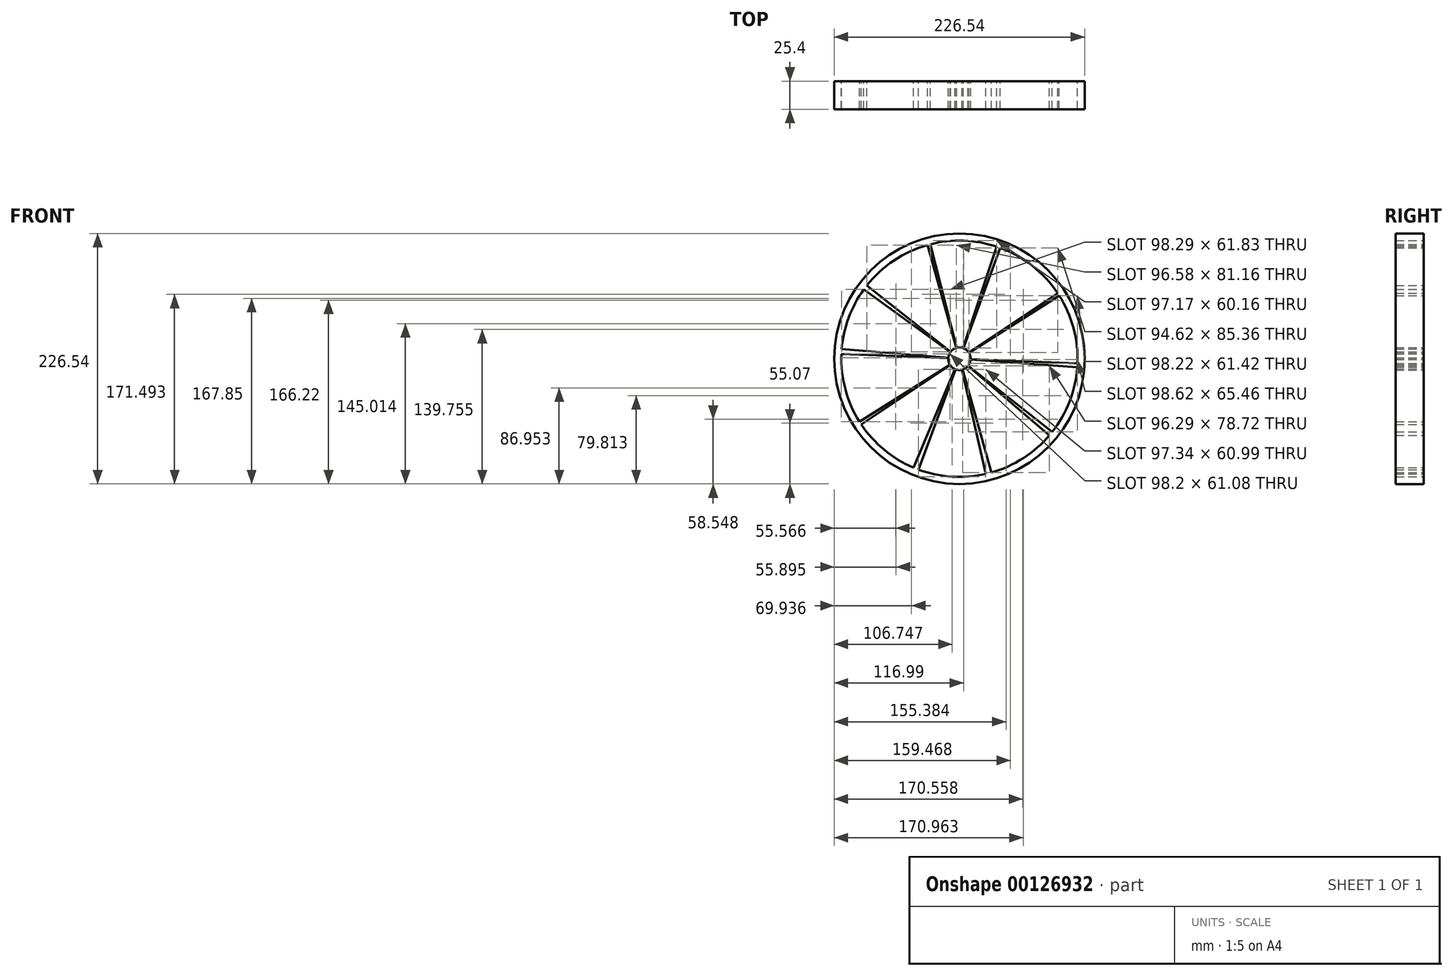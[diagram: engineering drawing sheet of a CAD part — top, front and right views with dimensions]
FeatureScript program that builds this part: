
annotation { "Feature Type Name" : "Feature", "Feature Type Description" : "" }
export const myFeature = defineFeature(function(context is Context, id is Id, definition is map)
    precondition{}
    {
        {
            var Q0;
            Q0=qCreatedBy(makeId("Front.planeOp"),FACE);
            var sketch = newSketch(context, id + "F0", { "sketchPlane" : qUnion([Q0])});
            skCircle(sketch, "E0", {"center": v(0, 0) * mm, "radius": 10.16 * mm});
            skCircle(sketch, "E1.cCircle", {"center": v(0, 0) * mm, "radius": 107.5 * mm, "construction": true});
            skLineSegment(sketch, "E1.0", {"start": v(-104.75, -29.51) * mm, "end": v(-108.75, 4.3) * mm});
            skLineSegment(sketch, "E1.1", {"start": v(-108.75, 4.3) * mm, "end": v(-102.1, 37.7) * mm});
            skLineSegment(sketch, "E1.2", {"start": v(-102.1, 37.7) * mm, "end": v(-85.45, 67.4) * mm});
            skLineSegment(sketch, "E1.3", {"start": v(-85.45, 67.4) * mm, "end": v(-60.44, 90.5) * mm});
            skLineSegment(sketch, "E1.4", {"start": v(-60.44, 90.5) * mm, "end": v(-29.51, 104.75) * mm});
            skLineSegment(sketch, "E1.5", {"start": v(-29.51, 104.75) * mm, "end": v(4.3, 108.75) * mm});
            skLineSegment(sketch, "E1.6", {"start": v(4.3, 108.75) * mm, "end": v(37.7, 102.1) * mm});
            skLineSegment(sketch, "E1.7", {"start": v(37.7, 102.1) * mm, "end": v(67.4, 85.45) * mm});
            skLineSegment(sketch, "E1.8", {"start": v(67.4, 85.45) * mm, "end": v(90.5, 60.44) * mm});
            skLineSegment(sketch, "E1.9", {"start": v(90.5, 60.44) * mm, "end": v(104.75, 29.51) * mm});
            skLineSegment(sketch, "E1.10", {"start": v(104.75, 29.51) * mm, "end": v(108.75, -4.3) * mm});
            skLineSegment(sketch, "E1.11", {"start": v(108.75, -4.3) * mm, "end": v(102.1, -37.7) * mm});
            skLineSegment(sketch, "E1.12", {"start": v(102.1, -37.7) * mm, "end": v(85.45, -67.4) * mm});
            skLineSegment(sketch, "E1.13", {"start": v(85.45, -67.4) * mm, "end": v(60.44, -90.5) * mm});
            skLineSegment(sketch, "E1.14", {"start": v(60.44, -90.5) * mm, "end": v(29.51, -104.75) * mm});
            skLineSegment(sketch, "E1.15", {"start": v(29.51, -104.75) * mm, "end": v(-4.3, -108.75) * mm});
            skLineSegment(sketch, "E1.16", {"start": v(-4.3, -108.75) * mm, "end": v(-37.7, -102.1) * mm});
            skLineSegment(sketch, "E1.17", {"start": v(-37.7, -102.1) * mm, "end": v(-67.4, -85.45) * mm});
            skLineSegment(sketch, "E1.18", {"start": v(-67.4, -85.45) * mm, "end": v(-90.5, -60.44) * mm});
            skLineSegment(sketch, "E1.19", {"start": v(-90.5, -60.44) * mm, "end": v(-104.75, -29.51) * mm});
            skPoint(sketch, "E1.0.midPoint", {"position": v(-106.75, -12.6) * mm});
            skCircle(sketch, "E2", {"center": v(0, 0) * mm, "radius": 106.87 * mm});
            skCircle(sketch, "E3", {"center": v(0, 0) * mm, "radius": 113.27 * mm});
            skLineSegment(sketch, "E4", {"start": v(-29.51, 104.75) * mm, "end": v(0, 0) * mm});
            skLineSegment(sketch, "E5", {"start": v(0, 0) * mm, "end": v(-26.74, 105.08) * mm});
            skLineSegment(sketch, "E6", {"start": v(37.7, 102.1) * mm, "end": v(0, 0) * mm});
            skLineSegment(sketch, "E7", {"start": v(0, 0) * mm, "end": v(34.26, 102.78) * mm});
            skLineSegment(sketch, "E8", {"start": v(0, 0) * mm, "end": v(90.5, 60.44) * mm});
            skLineSegment(sketch, "E9", {"start": v(0, 0) * mm, "end": v(91.61, 58.04) * mm});
            skLineSegment(sketch, "E10", {"start": v(0, 0) * mm, "end": v(108.75, -4.3) * mm});
            skLineSegment(sketch, "E11", {"start": v(0, 0) * mm, "end": v(108.06, -7.76) * mm});
            skLineSegment(sketch, "E12", {"start": v(0, 0) * mm, "end": v(85.45, -67.4) * mm});
            skLineSegment(sketch, "E13", {"start": v(0, 0) * mm, "end": v(81.47, -69.17) * mm});
            skLineSegment(sketch, "E14", {"start": v(0, 0) * mm, "end": v(29.51, -104.75) * mm});
            skLineSegment(sketch, "E15", {"start": v(0, 0) * mm, "end": v(24.1, -104.75) * mm});
            skLineSegment(sketch, "E16", {"start": v(0, 0) * mm, "end": v(-37.7, -102.1) * mm});
            skLineSegment(sketch, "E17", {"start": v(0, 0) * mm, "end": v(-41.43, -98.52) * mm});
            skLineSegment(sketch, "E18", {"start": v(0, 0) * mm, "end": v(-90.5, -60.44) * mm});
            skLineSegment(sketch, "E19", {"start": v(0, 0) * mm, "end": v(-91.78, -57.67) * mm});
            skLineSegment(sketch, "E20", {"start": v(0, 0) * mm, "end": v(-85.45, 67.4) * mm});
            skLineSegment(sketch, "E21", {"start": v(0, 0) * mm, "end": v(-87.67, 63.45) * mm});
            skLineSegment(sketch, "E22", {"start": v(0, 0) * mm, "end": v(-108.75, 4.3) * mm});
            skLineSegment(sketch, "E23", {"start": v(0, 0) * mm, "end": v(-107.85, 8.8) * mm});
            skSolve(sketch);
        }
        {
            var Q0;
            {var subQ0=sQuery(id+"F0.wireOp",EDGE,"E8");var subQ1=sQuery(id+"F0.wireOp",EDGE,"E0");var subQ2=makeQuery(id+"F0.imprint","INTERSECT",VERTEX,{"derivedFrom":[subQ1,subQ0]});Q0=makeQuery(id+"F0.imprint","IMPRINT",FACE,{"disambiguationData":[TD([[makeQuery(id+"F0.imprint","IMPRINT",EDGE,{"disambiguationData":[TD([[subQ2,-1.0]])],"derivedFrom":subQ1}),1.0]])]});}
            var Q1;
            {var subQ0=sQuery(id+"F0.wireOp",EDGE,"E7");var subQ1=sQuery(id+"F0.wireOp",EDGE,"E0");var subQ2=makeQuery(id+"F0.imprint","INTERSECT",VERTEX,{"derivedFrom":[subQ1,subQ0]});Q1=makeQuery(id+"F0.imprint","IMPRINT",FACE,{"disambiguationData":[TD([[makeQuery(id+"F0.imprint","IMPRINT",EDGE,{"disambiguationData":[TD([[subQ2,-1.0]])],"derivedFrom":subQ1}),1.0]])]});}
            var Q2;
            {var subQ0=sQuery(id+"F0.wireOp",EDGE,"E4");var subQ1=sQuery(id+"F0.wireOp",EDGE,"E0");var subQ2=makeQuery(id+"F0.imprint","INTERSECT",VERTEX,{"derivedFrom":[subQ1,subQ0]});Q2=makeQuery(id+"F0.imprint","IMPRINT",FACE,{"disambiguationData":[TD([[makeQuery(id+"F0.imprint","IMPRINT",EDGE,{"disambiguationData":[TD([[subQ2,-1.0]])],"derivedFrom":subQ1}),1.0]])]});}
            var Q3;
            {var subQ0=sQuery(id+"F0.wireOp",EDGE,"E21");var subQ1=sQuery(id+"F0.wireOp",EDGE,"E0");var subQ2=makeQuery(id+"F0.imprint","INTERSECT",VERTEX,{"derivedFrom":[subQ1,subQ0]});Q3=makeQuery(id+"F0.imprint","IMPRINT",FACE,{"disambiguationData":[TD([[makeQuery(id+"F0.imprint","IMPRINT",EDGE,{"disambiguationData":[TD([[subQ2,-1.0]])],"derivedFrom":subQ1}),1.0]])]});}
            var Q4;
            {var subQ0=sQuery(id+"F0.wireOp",EDGE,"E22");var subQ1=sQuery(id+"F0.wireOp",EDGE,"E0");var subQ2=makeQuery(id+"F0.imprint","INTERSECT",VERTEX,{"derivedFrom":[subQ1,subQ0]});Q4=makeQuery(id+"F0.imprint","IMPRINT",FACE,{"disambiguationData":[TD([[makeQuery(id+"F0.imprint","IMPRINT",EDGE,{"disambiguationData":[TD([[subQ2,-1.0]])],"derivedFrom":subQ1}),1.0]])]});}
            var Q5;
            {var subQ0=sQuery(id+"F0.wireOp",EDGE,"E16");var subQ1=sQuery(id+"F0.wireOp",EDGE,"E0");var subQ2=makeQuery(id+"F0.imprint","INTERSECT",VERTEX,{"derivedFrom":[subQ1,subQ0]});Q5=makeQuery(id+"F0.imprint","IMPRINT",FACE,{"disambiguationData":[TD([[makeQuery(id+"F0.imprint","IMPRINT",EDGE,{"disambiguationData":[TD([[subQ2,-1.0]])],"derivedFrom":subQ1}),1.0]])]});}
            var Q6;
            {var subQ0=sQuery(id+"F0.wireOp",EDGE,"E14");var subQ1=sQuery(id+"F0.wireOp",EDGE,"E0");var subQ2=makeQuery(id+"F0.imprint","INTERSECT",VERTEX,{"derivedFrom":[subQ1,subQ0]});Q6=makeQuery(id+"F0.imprint","IMPRINT",FACE,{"disambiguationData":[TD([[makeQuery(id+"F0.imprint","IMPRINT",EDGE,{"disambiguationData":[TD([[subQ2,-1.0]])],"derivedFrom":subQ1}),1.0]])]});}
            var Q7;
            {var subQ0=sQuery(id+"F0.wireOp",EDGE,"E12");var subQ1=sQuery(id+"F0.wireOp",EDGE,"E0");var subQ2=makeQuery(id+"F0.imprint","INTERSECT",VERTEX,{"derivedFrom":[subQ1,subQ0]});Q7=makeQuery(id+"F0.imprint","IMPRINT",FACE,{"disambiguationData":[TD([[makeQuery(id+"F0.imprint","IMPRINT",EDGE,{"disambiguationData":[TD([[subQ2,-1.0]])],"derivedFrom":subQ1}),1.0]])]});}
            var Q8;
            {var subQ0=sQuery(id+"F0.wireOp",EDGE,"E5");var subQ1=sQuery(id+"F0.wireOp",EDGE,"E0");var subQ2=makeQuery(id+"F0.imprint","INTERSECT",VERTEX,{"derivedFrom":[subQ1,subQ0]});Q8=makeQuery(id+"F0.imprint","IMPRINT",FACE,{"disambiguationData":[TD([[makeQuery(id+"F0.imprint","IMPRINT",EDGE,{"disambiguationData":[TD([[subQ2,-1.0]])],"derivedFrom":subQ1}),1.0]])]});}
            var Q9;
            {var subQ0=sQuery(id+"F0.wireOp",EDGE,"E20");var subQ1=sQuery(id+"F0.wireOp",EDGE,"E0");var subQ2=makeQuery(id+"F0.imprint","INTERSECT",VERTEX,{"derivedFrom":[subQ1,subQ0]});Q9=makeQuery(id+"F0.imprint","IMPRINT",FACE,{"disambiguationData":[TD([[makeQuery(id+"F0.imprint","IMPRINT",EDGE,{"disambiguationData":[TD([[subQ2,-1.0]])],"derivedFrom":subQ1}),1.0]])]});}
            var Q10;
            {var subQ0=sQuery(id+"F0.wireOp",EDGE,"E23");var subQ1=sQuery(id+"F0.wireOp",EDGE,"E0");var subQ2=makeQuery(id+"F0.imprint","INTERSECT",VERTEX,{"derivedFrom":[subQ1,subQ0]});Q10=makeQuery(id+"F0.imprint","IMPRINT",FACE,{"disambiguationData":[TD([[makeQuery(id+"F0.imprint","IMPRINT",EDGE,{"disambiguationData":[TD([[subQ2,-1.0]])],"derivedFrom":subQ1}),1.0]])]});}
            var Q11;
            {var subQ0=sQuery(id+"F0.wireOp",EDGE,"E19");var subQ1=sQuery(id+"F0.wireOp",EDGE,"E0");var subQ2=makeQuery(id+"F0.imprint","INTERSECT",VERTEX,{"derivedFrom":[subQ1,subQ0]});Q11=makeQuery(id+"F0.imprint","IMPRINT",FACE,{"disambiguationData":[TD([[makeQuery(id+"F0.imprint","IMPRINT",EDGE,{"disambiguationData":[TD([[subQ2,-1.0]])],"derivedFrom":subQ1}),1.0]])]});}
            var Q12;
            {var subQ0=sQuery(id+"F0.wireOp",EDGE,"E18");var subQ1=sQuery(id+"F0.wireOp",EDGE,"E0");var subQ2=makeQuery(id+"F0.imprint","INTERSECT",VERTEX,{"derivedFrom":[subQ1,subQ0]});Q12=makeQuery(id+"F0.imprint","IMPRINT",FACE,{"disambiguationData":[TD([[makeQuery(id+"F0.imprint","IMPRINT",EDGE,{"disambiguationData":[TD([[subQ2,-1.0]])],"derivedFrom":subQ1}),1.0]])]});}
            var Q13;
            {var subQ0=sQuery(id+"F0.wireOp",EDGE,"E15");var subQ1=sQuery(id+"F0.wireOp",EDGE,"E0");var subQ2=makeQuery(id+"F0.imprint","INTERSECT",VERTEX,{"derivedFrom":[subQ1,subQ0]});Q13=makeQuery(id+"F0.imprint","IMPRINT",FACE,{"disambiguationData":[TD([[makeQuery(id+"F0.imprint","IMPRINT",EDGE,{"disambiguationData":[TD([[subQ2,-1.0]])],"derivedFrom":subQ1}),1.0]])]});}
            var Q14;
            {var subQ0=sQuery(id+"F0.wireOp",EDGE,"E17");var subQ1=sQuery(id+"F0.wireOp",EDGE,"E0");var subQ2=makeQuery(id+"F0.imprint","INTERSECT",VERTEX,{"derivedFrom":[subQ1,subQ0]});Q14=makeQuery(id+"F0.imprint","IMPRINT",FACE,{"disambiguationData":[TD([[makeQuery(id+"F0.imprint","IMPRINT",EDGE,{"disambiguationData":[TD([[subQ2,-1.0]])],"derivedFrom":subQ1}),1.0]])]});}
            var Q15;
            {var subQ0=sQuery(id+"F0.wireOp",EDGE,"E13");var subQ1=sQuery(id+"F0.wireOp",EDGE,"E0");var subQ2=makeQuery(id+"F0.imprint","INTERSECT",VERTEX,{"derivedFrom":[subQ1,subQ0]});Q15=makeQuery(id+"F0.imprint","IMPRINT",FACE,{"disambiguationData":[TD([[makeQuery(id+"F0.imprint","IMPRINT",EDGE,{"disambiguationData":[TD([[subQ2,-1.0]])],"derivedFrom":subQ1}),1.0]])]});}
            var Q16;
            {var subQ0=sQuery(id+"F0.wireOp",EDGE,"E11");var subQ1=sQuery(id+"F0.wireOp",EDGE,"E0");var subQ2=makeQuery(id+"F0.imprint","INTERSECT",VERTEX,{"derivedFrom":[subQ1,subQ0]});Q16=makeQuery(id+"F0.imprint","IMPRINT",FACE,{"disambiguationData":[TD([[makeQuery(id+"F0.imprint","IMPRINT",EDGE,{"disambiguationData":[TD([[subQ2,-1.0]])],"derivedFrom":subQ1}),1.0]])]});}
            var Q17;
            {var subQ0=sQuery(id+"F0.wireOp",EDGE,"E9");var subQ1=sQuery(id+"F0.wireOp",EDGE,"E0");var subQ2=makeQuery(id+"F0.imprint","INTERSECT",VERTEX,{"derivedFrom":[subQ1,subQ0]});Q17=makeQuery(id+"F0.imprint","IMPRINT",FACE,{"disambiguationData":[TD([[makeQuery(id+"F0.imprint","IMPRINT",EDGE,{"disambiguationData":[TD([[subQ2,1.0]])],"derivedFrom":subQ1}),1.0]])]});}
            var Q18;
            {var subQ0=sQuery(id+"F0.wireOp",EDGE,"E8");var subQ1=sQuery(id+"F0.wireOp",EDGE,"E0");var subQ2=makeQuery(id+"F0.imprint","INTERSECT",VERTEX,{"derivedFrom":[subQ1,subQ0]});Q18=makeQuery(id+"F0.imprint","IMPRINT",FACE,{"disambiguationData":[TD([[makeQuery(id+"F0.imprint","IMPRINT",EDGE,{"disambiguationData":[TD([[subQ2,1.0]])],"derivedFrom":subQ1}),1.0]])]});}
            var Q19;
            {var subQ0=sQuery(id+"F0.wireOp",EDGE,"E6");var subQ1=sQuery(id+"F0.wireOp",EDGE,"E0");var subQ2=makeQuery(id+"F0.imprint","INTERSECT",VERTEX,{"derivedFrom":[subQ1,subQ0]});Q19=makeQuery(id+"F0.imprint","IMPRINT",FACE,{"disambiguationData":[TD([[makeQuery(id+"F0.imprint","IMPRINT",EDGE,{"disambiguationData":[TD([[subQ2,-1.0]])],"derivedFrom":subQ1}),1.0]])]});}
            extrude(context, id + "F1", {"entities" : qUnion([Q0, Q1, Q2, Q3, Q4, Q5, Q6, Q7, Q8, Q9, Q10, Q11, Q12, Q13, Q14, Q15, Q16, Q17, Q18, Q19]), "depth" : 25.4 * mm});
        }
        {
            var Q0;
            {var subQ8=sQuery(id+"F0.wireOp",EDGE,"E1.0");Q0=makeQuery(id+"F0.imprint","IMPRINT",FACE,{"disambiguationData":[TD([[makeQuery(id+"F0.imprint","IMPRINT",EDGE,{"derivedFrom":subQ8}),1.0]])]});}
            var Q1;
            {var subQ0=sQuery(id+"F0.wireOp",EDGE,"E20");var subQ1=sQuery(id+"F0.wireOp",EDGE,"E0");var subQ2=makeQuery(id+"F0.imprint","INTERSECT",VERTEX,{"derivedFrom":[subQ1,subQ0]});Q1=makeQuery(id+"F0.imprint","IMPRINT",FACE,{"disambiguationData":[TD([[makeQuery(id+"F0.imprint","IMPRINT",EDGE,{"disambiguationData":[TD([[subQ2,-1.0]])],"derivedFrom":subQ1}),-1.0]])]});}
            var Q2;
            {var subQ0=sQuery(id+"F0.wireOp",EDGE,"E5");var subQ1=sQuery(id+"F0.wireOp",EDGE,"E0");var subQ2=makeQuery(id+"F0.imprint","INTERSECT",VERTEX,{"derivedFrom":[subQ1,subQ0]});Q2=makeQuery(id+"F0.imprint","IMPRINT",FACE,{"disambiguationData":[TD([[makeQuery(id+"F0.imprint","IMPRINT",EDGE,{"disambiguationData":[TD([[subQ2,-1.0]])],"derivedFrom":subQ1}),-1.0]])]});}
            var Q3;
            {var subQ0=sQuery(id+"F0.wireOp",EDGE,"E6");var subQ1=sQuery(id+"F0.wireOp",EDGE,"E0");var subQ2=makeQuery(id+"F0.imprint","INTERSECT",VERTEX,{"derivedFrom":[subQ1,subQ0]});Q3=makeQuery(id+"F0.imprint","IMPRINT",FACE,{"disambiguationData":[TD([[makeQuery(id+"F0.imprint","IMPRINT",EDGE,{"disambiguationData":[TD([[subQ2,-1.0]])],"derivedFrom":subQ1}),-1.0]])]});}
            var Q4;
            {var subQ0=sQuery(id+"F0.wireOp",EDGE,"E8");var subQ1=sQuery(id+"F0.wireOp",EDGE,"E0");var subQ2=makeQuery(id+"F0.imprint","INTERSECT",VERTEX,{"derivedFrom":[subQ1,subQ0]});Q4=makeQuery(id+"F0.imprint","IMPRINT",FACE,{"disambiguationData":[TD([[makeQuery(id+"F0.imprint","IMPRINT",EDGE,{"disambiguationData":[TD([[subQ2,1.0]])],"derivedFrom":subQ1}),-1.0]])]});}
            var Q5;
            {var subQ0=sQuery(id+"F0.wireOp",EDGE,"E11");var subQ1=sQuery(id+"F0.wireOp",EDGE,"E0");var subQ2=makeQuery(id+"F0.imprint","INTERSECT",VERTEX,{"derivedFrom":[subQ1,subQ0]});Q5=makeQuery(id+"F0.imprint","IMPRINT",FACE,{"disambiguationData":[TD([[makeQuery(id+"F0.imprint","IMPRINT",EDGE,{"disambiguationData":[TD([[subQ2,-1.0]])],"derivedFrom":subQ1}),-1.0]])]});}
            var Q6;
            {var subQ0=sQuery(id+"F0.wireOp",EDGE,"E13");var subQ1=sQuery(id+"F0.wireOp",EDGE,"E0");var subQ2=makeQuery(id+"F0.imprint","INTERSECT",VERTEX,{"derivedFrom":[subQ1,subQ0]});Q6=makeQuery(id+"F0.imprint","IMPRINT",FACE,{"disambiguationData":[TD([[makeQuery(id+"F0.imprint","IMPRINT",EDGE,{"disambiguationData":[TD([[subQ2,-1.0]])],"derivedFrom":subQ1}),-1.0]])]});}
            var Q7;
            {var subQ0=sQuery(id+"F0.wireOp",EDGE,"E15");var subQ1=sQuery(id+"F0.wireOp",EDGE,"E0");var subQ2=makeQuery(id+"F0.imprint","INTERSECT",VERTEX,{"derivedFrom":[subQ1,subQ0]});Q7=makeQuery(id+"F0.imprint","IMPRINT",FACE,{"disambiguationData":[TD([[makeQuery(id+"F0.imprint","IMPRINT",EDGE,{"disambiguationData":[TD([[subQ2,-1.0]])],"derivedFrom":subQ1}),-1.0]])]});}
            var Q8;
            {var subQ0=sQuery(id+"F0.wireOp",EDGE,"E17");var subQ1=sQuery(id+"F0.wireOp",EDGE,"E0");var subQ2=makeQuery(id+"F0.imprint","INTERSECT",VERTEX,{"derivedFrom":[subQ1,subQ0]});Q8=makeQuery(id+"F0.imprint","IMPRINT",FACE,{"disambiguationData":[TD([[makeQuery(id+"F0.imprint","IMPRINT",EDGE,{"disambiguationData":[TD([[subQ2,-1.0]])],"derivedFrom":subQ1}),-1.0]])]});}
            var Q9;
            {var subQ0=sQuery(id+"F0.wireOp",EDGE,"E19");var subQ1=sQuery(id+"F0.wireOp",EDGE,"E0");var subQ2=makeQuery(id+"F0.imprint","INTERSECT",VERTEX,{"derivedFrom":[subQ1,subQ0]});Q9=makeQuery(id+"F0.imprint","IMPRINT",FACE,{"disambiguationData":[TD([[makeQuery(id+"F0.imprint","IMPRINT",EDGE,{"disambiguationData":[TD([[subQ2,-1.0]])],"derivedFrom":subQ1}),-1.0]])]});}
            var Q10;
            {var subQ0=sQuery(id+"F0.wireOp",EDGE,"E23");var subQ1=sQuery(id+"F0.wireOp",EDGE,"E0");var subQ2=makeQuery(id+"F0.imprint","INTERSECT",VERTEX,{"derivedFrom":[subQ1,subQ0]});Q10=makeQuery(id+"F0.imprint","IMPRINT",FACE,{"disambiguationData":[TD([[makeQuery(id+"F0.imprint","IMPRINT",EDGE,{"disambiguationData":[TD([[subQ2,-1.0]])],"derivedFrom":subQ1}),-1.0]])]});}
            var Q11;
            {var subQ0=sQuery(id+"F0.wireOp",EDGE,"E20");var subQ5=sQuery(id+"F0.wireOp",EDGE,"E2");var subQ6=makeQuery(id+"F0.imprint","INTERSECT",VERTEX,{"derivedFrom":[subQ5,subQ0]});Q11=makeQuery(id+"F0.imprint","IMPRINT",FACE,{"disambiguationData":[TD([[makeQuery(id+"F0.imprint","IMPRINT",EDGE,{"disambiguationData":[TD([[subQ6,-1.0]])],"derivedFrom":subQ5}),-1.0]])]});}
            var Q12;
            {var subQ3=sQuery(id+"F0.wireOp",EDGE,"E23");var subQ5=sQuery(id+"F0.wireOp",EDGE,"E2");var subQ6=makeQuery(id+"F0.imprint","INTERSECT",VERTEX,{"derivedFrom":[subQ5,subQ3]});Q12=makeQuery(id+"F0.imprint","IMPRINT",FACE,{"disambiguationData":[TD([[makeQuery(id+"F0.imprint","IMPRINT",EDGE,{"disambiguationData":[TD([[subQ6,-1.0]])],"derivedFrom":subQ5}),-1.0]])]});}
            var Q13;
            {var subQ5=sQuery(id+"F0.wireOp",EDGE,"E1.2");var subQ6=sQuery(id+"F0.wireOp",EDGE,"E1.1");var subQ7=makeQuery(id+"F0.imprint","INTERSECT",VERTEX,{"derivedFrom":[subQ6,subQ5]});Q13=makeQuery(id+"F0.imprint","IMPRINT",FACE,{"disambiguationData":[TD([[makeQuery(id+"F0.imprint","IMPRINT",EDGE,{"disambiguationData":[TD([[subQ7,1.0]])],"derivedFrom":subQ6}),-1.0]])]});}
            var Q14;
            {var subQ6=sQuery(id+"F0.wireOp",EDGE,"E1.0");Q14=makeQuery(id+"F0.imprint","IMPRINT",FACE,{"disambiguationData":[TD([[makeQuery(id+"F0.imprint","IMPRINT",EDGE,{"derivedFrom":subQ6}),-1.0]])]});}
            var Q15;
            {var subQ3=sQuery(id+"F0.wireOp",EDGE,"E19");var subQ5=sQuery(id+"F0.wireOp",EDGE,"E2");var subQ6=makeQuery(id+"F0.imprint","INTERSECT",VERTEX,{"derivedFrom":[subQ5,subQ3]});Q15=makeQuery(id+"F0.imprint","IMPRINT",FACE,{"disambiguationData":[TD([[makeQuery(id+"F0.imprint","IMPRINT",EDGE,{"disambiguationData":[TD([[subQ6,-1.0]])],"derivedFrom":subQ5}),-1.0]])]});}
            var Q16;
            {var subQ7=sQuery(id+"F0.wireOp",EDGE,"E1.17");Q16=makeQuery(id+"F0.imprint","IMPRINT",FACE,{"disambiguationData":[TD([[makeQuery(id+"F0.imprint","IMPRINT",EDGE,{"derivedFrom":subQ7}),-1.0]])]});}
            var Q17;
            {var subQ4=sQuery(id+"F0.wireOp",EDGE,"E1.15");Q17=makeQuery(id+"F0.imprint","IMPRINT",FACE,{"disambiguationData":[TD([[makeQuery(id+"F0.imprint","IMPRINT",EDGE,{"derivedFrom":subQ4}),-1.0]])]});}
            var Q18;
            {var subQ4=sQuery(id+"F0.wireOp",EDGE,"E1.13");Q18=makeQuery(id+"F0.imprint","IMPRINT",FACE,{"disambiguationData":[TD([[makeQuery(id+"F0.imprint","IMPRINT",EDGE,{"derivedFrom":subQ4}),-1.0]])]});}
            var Q19;
            {var subQ5=sQuery(id+"F0.wireOp",EDGE,"E1.12");Q19=makeQuery(id+"F0.imprint","IMPRINT",FACE,{"disambiguationData":[TD([[makeQuery(id+"F0.imprint","IMPRINT",EDGE,{"derivedFrom":subQ5}),-1.0]])]});}
            var Q20;
            {var subQ7=sQuery(id+"F0.wireOp",EDGE,"E1.10");Q20=makeQuery(id+"F0.imprint","IMPRINT",FACE,{"disambiguationData":[TD([[makeQuery(id+"F0.imprint","IMPRINT",EDGE,{"derivedFrom":subQ7}),-1.0]])]});}
            var Q21;
            {var subQ3=sQuery(id+"F0.wireOp",EDGE,"E11");var subQ5=sQuery(id+"F0.wireOp",EDGE,"E2");var subQ6=makeQuery(id+"F0.imprint","INTERSECT",VERTEX,{"derivedFrom":[subQ5,subQ3]});Q21=makeQuery(id+"F0.imprint","IMPRINT",FACE,{"disambiguationData":[TD([[makeQuery(id+"F0.imprint","IMPRINT",EDGE,{"disambiguationData":[TD([[subQ6,-1.0]])],"derivedFrom":subQ5}),-1.0]])]});}
            var Q22;
            {var subQ0=sQuery(id+"F0.wireOp",EDGE,"E8");var subQ5=sQuery(id+"F0.wireOp",EDGE,"E2");var subQ7=makeQuery(id+"F0.imprint","INTERSECT",VERTEX,{"derivedFrom":[subQ5,subQ0]});Q22=makeQuery(id+"F0.imprint","IMPRINT",FACE,{"disambiguationData":[TD([[makeQuery(id+"F0.imprint","IMPRINT",EDGE,{"disambiguationData":[TD([[subQ7,1.0]])],"derivedFrom":subQ5}),-1.0]])]});}
            var Q23;
            {var subQ1=sQuery(id+"F0.wireOp",EDGE,"E1.7");Q23=makeQuery(id+"F0.imprint","IMPRINT",FACE,{"disambiguationData":[TD([[makeQuery(id+"F0.imprint","IMPRINT",EDGE,{"derivedFrom":subQ1}),-1.0]])]});}
            var Q24;
            {var subQ0=sQuery(id+"F0.wireOp",EDGE,"E6");var subQ5=sQuery(id+"F0.wireOp",EDGE,"E2");var subQ6=makeQuery(id+"F0.imprint","INTERSECT",VERTEX,{"derivedFrom":[subQ5,subQ0]});Q24=makeQuery(id+"F0.imprint","IMPRINT",FACE,{"disambiguationData":[TD([[makeQuery(id+"F0.imprint","IMPRINT",EDGE,{"disambiguationData":[TD([[subQ6,-1.0]])],"derivedFrom":subQ5}),-1.0]])]});}
            var Q25;
            {var subQ5=sQuery(id+"F0.wireOp",EDGE,"E1.5");var subQ7=sQuery(id+"F0.wireOp",EDGE,"E1.6");var subQ8=makeQuery(id+"F0.imprint","INTERSECT",VERTEX,{"derivedFrom":[subQ5,subQ7]});Q25=makeQuery(id+"F0.imprint","IMPRINT",FACE,{"disambiguationData":[TD([[makeQuery(id+"F0.imprint","IMPRINT",EDGE,{"disambiguationData":[TD([[subQ8,1.0]])],"derivedFrom":subQ5}),-1.0]])]});}
            var Q26;
            {var subQ6=sQuery(id+"F0.wireOp",EDGE,"E1.3");Q26=makeQuery(id+"F0.imprint","IMPRINT",FACE,{"disambiguationData":[TD([[makeQuery(id+"F0.imprint","IMPRINT",EDGE,{"derivedFrom":subQ6}),-1.0]])]});}
            var Q27;
            {var subQ3=sQuery(id+"F0.wireOp",EDGE,"E5");var subQ5=sQuery(id+"F0.wireOp",EDGE,"E2");var subQ6=makeQuery(id+"F0.imprint","INTERSECT",VERTEX,{"derivedFrom":[subQ5,subQ3]});Q27=makeQuery(id+"F0.imprint","IMPRINT",FACE,{"disambiguationData":[TD([[makeQuery(id+"F0.imprint","IMPRINT",EDGE,{"disambiguationData":[TD([[subQ6,-1.0]])],"derivedFrom":subQ5}),-1.0]])]});}
            extrude(context, id + "F2", {"entities" : qUnion([Q0, Q1, Q2, Q3, Q4, Q5, Q6, Q7, Q8, Q9, Q10, Q11, Q12, Q13, Q14, Q15, Q16, Q17, Q18, Q19, Q20, Q21, Q22, Q23, Q24, Q25, Q26, Q27]), "operationType" : NewBodyOperationType.ADD, "depth" : 25.4 * mm});
        }
    });
